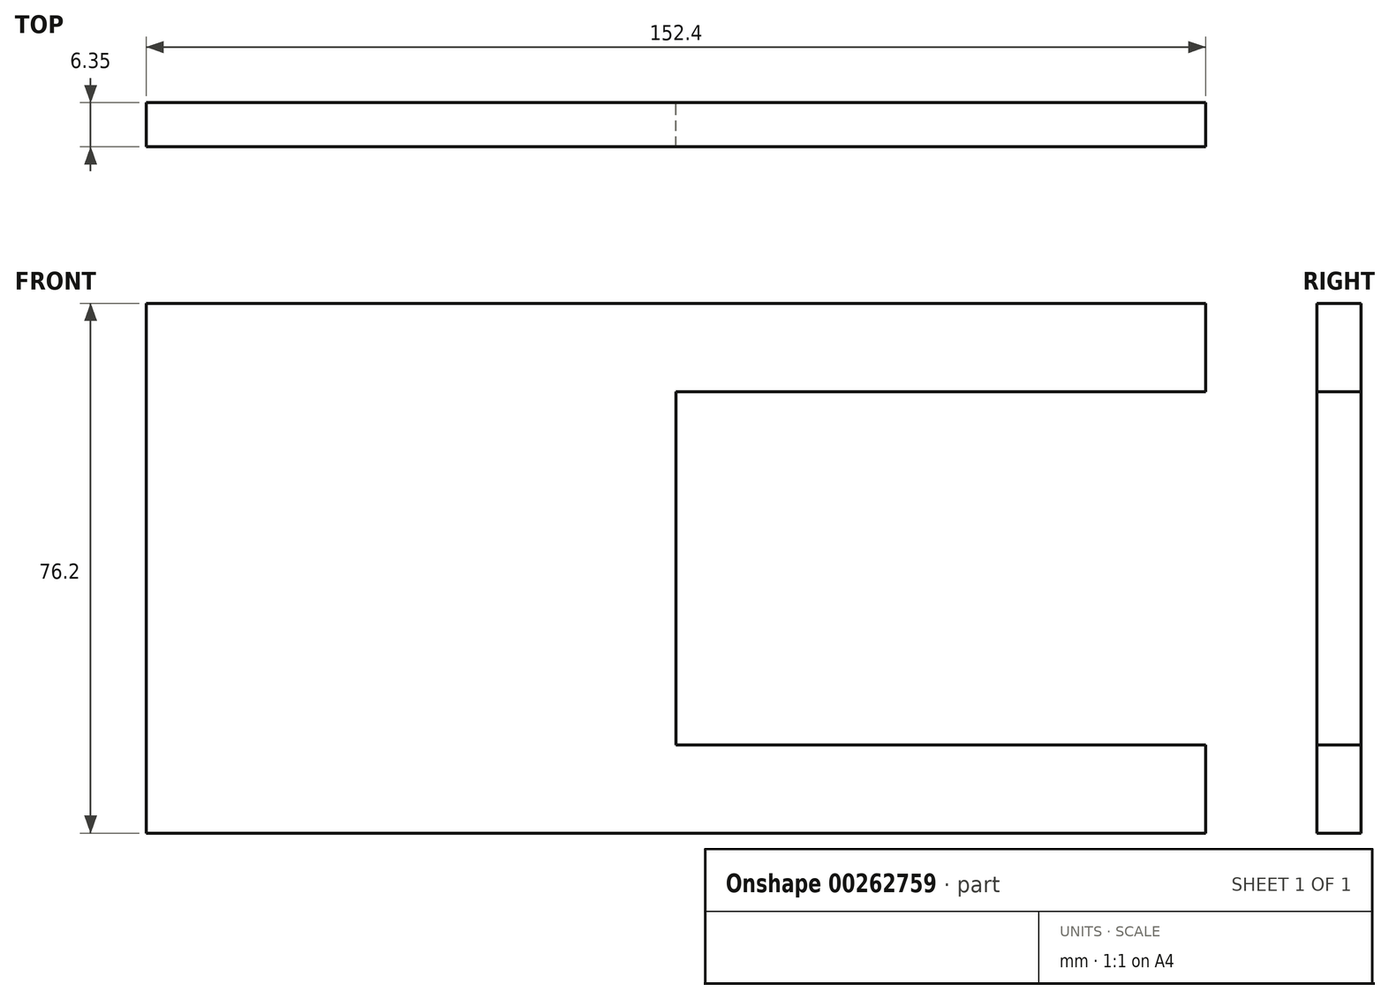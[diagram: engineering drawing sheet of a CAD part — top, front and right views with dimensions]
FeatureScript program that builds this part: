
annotation { "Feature Type Name" : "Feature", "Feature Type Description" : "" }
export const myFeature = defineFeature(function(context is Context, id is Id, definition is map)
    precondition{}
    {
        {
            var Q0;
            Q0=qCreatedBy(makeId("Front.planeOp"),FACE);
            var sketch = newSketch(context, id + "F0", { "sketchPlane" : qUnion([Q0])});
            skLineSegment(sketch, "E0.bottom", {"start": v(0, 0) * mm, "end": v(152.4, 0) * mm});
            skLineSegment(sketch, "E0.top", {"start": v(0, -76.2) * mm, "end": v(152.4, -76.2) * mm});
            skLineSegment(sketch, "E0.left", {"start": v(0, 0) * mm, "end": v(0, -76.2) * mm});
            skLineSegment(sketch, "E0.right", {"start": v(152.4, 0) * mm, "end": v(152.4, -12.7) * mm});
            skLineSegment(sketch, "E1.bottom", {"start": v(152.4, -12.7) * mm, "end": v(76.2, -12.7) * mm});
            skLineSegment(sketch, "E1.top", {"start": v(152.4, -63.5) * mm, "end": v(76.2, -63.5) * mm});
            skLineSegment(sketch, "E1.right", {"start": v(76.2, -12.7) * mm, "end": v(76.2, -63.5) * mm});
            skLineSegment(sketch, "E2.trimOffspring", {"start": v(152.4, -63.5) * mm, "end": v(152.4, -76.2) * mm});
            skSolve(sketch);
        }
        {
            var Q0;
            Q0=makeQuery(id+"F0.imprint","IMPRINT",FACE,{"disambiguationData":[TD([[makeQuery(id+"F0.imprint","IMPRINT",EDGE,{"derivedFrom":sQuery(id+"F0.wireOp",EDGE,"E0.bottom")}),-1.0]])]});
            extrude(context, id + "F1", {"entities" : qUnion([Q0]), "depth" : 6.35 * mm});
        }
    });
